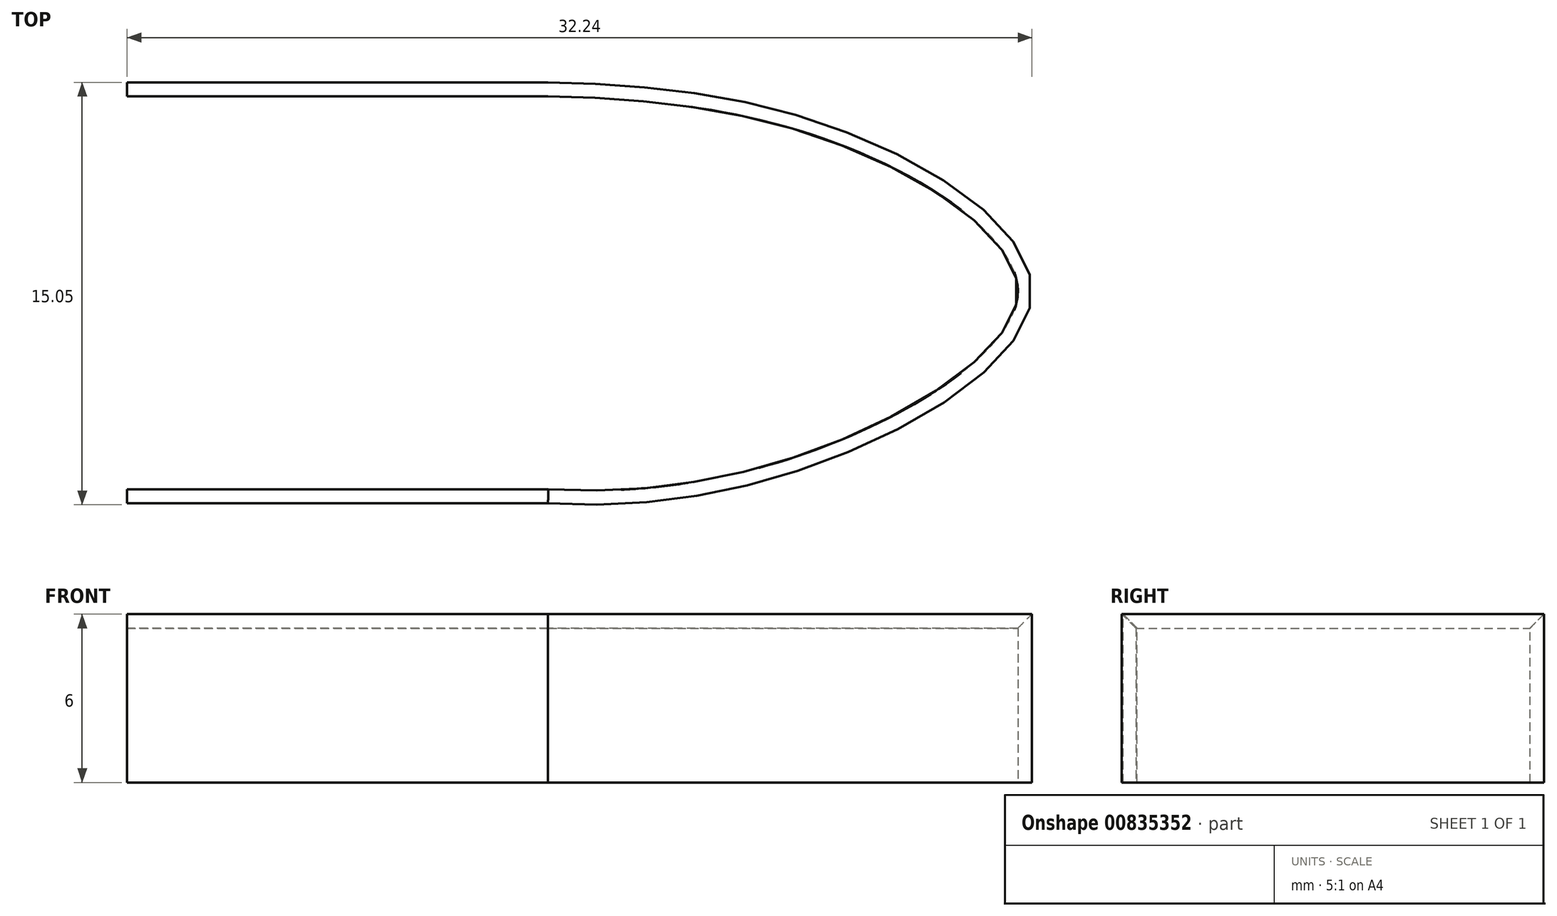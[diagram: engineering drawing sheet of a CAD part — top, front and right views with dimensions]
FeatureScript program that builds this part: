
annotation { "Feature Type Name" : "Feature", "Feature Type Description" : "" }
export const myFeature = defineFeature(function(context is Context, id is Id, definition is map)
    precondition{}
    {
        {
            var Q0;
            Q0=qCreatedBy(makeId("Top.planeOp"),FACE);
            var sketch = newSketch(context, id + "F0", { "sketchPlane" : qUnion([Q0])});
            skLineSegment(sketch, "E0", {"start": v(-13.75, 0) * mm, "end": v(17.96, 0) * mm, "construction": true});
            skLineSegment(sketch, "E1", {"start": v(-8.02, -4.91) * mm, "end": v(6.98, -4.91) * mm});
            skLineSegment(sketch, "E2", {"start": v(-8.02, -4.91) * mm, "end": v(-8.02, 10.09) * mm, "construction": true});
            skLineSegment(sketch, "E3", {"start": v(6.98, -4.91) * mm, "end": v(6.98, 10.09) * mm, "construction": true});
            skLineSegment(sketch, "E4", {"start": v(-8.02, 10.09) * mm, "end": v(6.98, 10.09) * mm});
            skFitSpline(sketch, "E5", {"points": [v(6.98, 10.09) * mm, v(17.83, 8.23) * mm, v(24.22, 2.66) * mm, v(17.96, -2.97) * mm, v(6.98, -4.91) * mm], "startDerivative": vector(38.27, -0.53) * mm, "endDerivative": vector(-39.69, 2.5) * mm});
            skLineSegment(sketch, "E6", {"start": v(-8.02, 2.59) * mm, "end": v(6.98, 2.59) * mm, "construction": true});
            skLineSegment(sketch, "E7", {"start": v(6.98, 2.59) * mm, "end": v(33, 2.59) * mm, "construction": true});
            skSolve(sketch);
        }
        {
            var Q0;
            Q0=sQuery(id+"F0.wireOp",EDGE,"E2");
            cPoint(context, id + "F1", {"entities" : qUnion([Q0]), "parameter" : 0.5});
        }
        {
            var Q0;
            Q0=qCreatedBy(makeId("Right.planeOp"),FACE);
            var Q1;
            Q1 = qCreatedBy(id + "F1" ,VERTEX);
            cPlane(context, id + "F2", {"entities" : qUnion([Q0, Q1]), "cplaneType" : CPlaneType.PLANE_POINT, "offset" : 25 * mm, "width" : 150 * mm, "height" : 150 * mm});
        }
        {
            var Q0;
            Q0=qCreatedBy(id+"F2.planeOp",FACE);
            var sketch = newSketch(context, id + "F3", { "sketchPlane" : qUnion([Q0])});
            skLineSegment(sketch, "E8.bottom", {"start": v(-4.91, 0) * mm, "end": v(-4.41, 0) * mm});
            skLineSegment(sketch, "E8.top", {"start": v(-4.91, 6) * mm, "end": v(-4.41, 6) * mm});
            skLineSegment(sketch, "E8.left", {"start": v(-4.91, 0) * mm, "end": v(-4.91, 6) * mm});
            skLineSegment(sketch, "E8.right", {"start": v(-4.41, 0) * mm, "end": v(-4.41, 6) * mm});
            skSolve(sketch);
        }
        {
            var Q0;
            Q0=makeQuery(id+"F3.imprint","IMPRINT",FACE,{"disambiguationData":[TD([[makeQuery(id+"F3.imprint","IMPRINT",EDGE,{"derivedFrom":sQuery(id+"F3.wireOp",EDGE,"E8.bottom")}),1.0]])]});
            var Q1;
            Q1=sQuery(id+"F0.wireOp",EDGE,"E1");
            var Q2;
            Q2=sQuery(id+"F0.wireOp",EDGE,"E5");
            var Q3;
            Q3=sQuery(id+"F0.wireOp",EDGE,"E4");
            sweep(context, id + "F4", {"profiles" : qUnion([Q0]), "path" : qUnion([Q1, Q2, Q3])});
        }
        {
            var Q0;
            Q0=makeQuery(id+"F4.opSweep","SWEPT_EDGE",EDGE,{"disambiguationData":[OSD([sQuery(id+"F0.wireOp",EDGE,"E1"),sQuery(id+"F3.wireOp",EDGE,"E8.top"),sQuery(id+"F3.wireOp",EDGE,"E8.right")])]});
            var Q1;
            Q1=makeQuery(id+"F4.opSweep","SWEPT_EDGE",EDGE,{"disambiguationData":[OSD([sQuery(id+"F0.wireOp",EDGE,"E5"),sQuery(id+"F3.wireOp",EDGE,"E8.top"),sQuery(id+"F3.wireOp",EDGE,"E8.right")]),OD(0.0)]});
            var Q2;
            Q2=makeQuery(id+"F4.opSweep","SWEPT_EDGE",EDGE,{"disambiguationData":[OSD([sQuery(id+"F0.wireOp",EDGE,"E4"),sQuery(id+"F3.wireOp",EDGE,"E8.top"),sQuery(id+"F3.wireOp",EDGE,"E8.right")])]});
            chamfer(context, id + "F5", {"entities" : qUnion([Q0, Q1, Q2]), "width" : 0.5 * mm, "tangentPropagation" : true});
        }
    });
